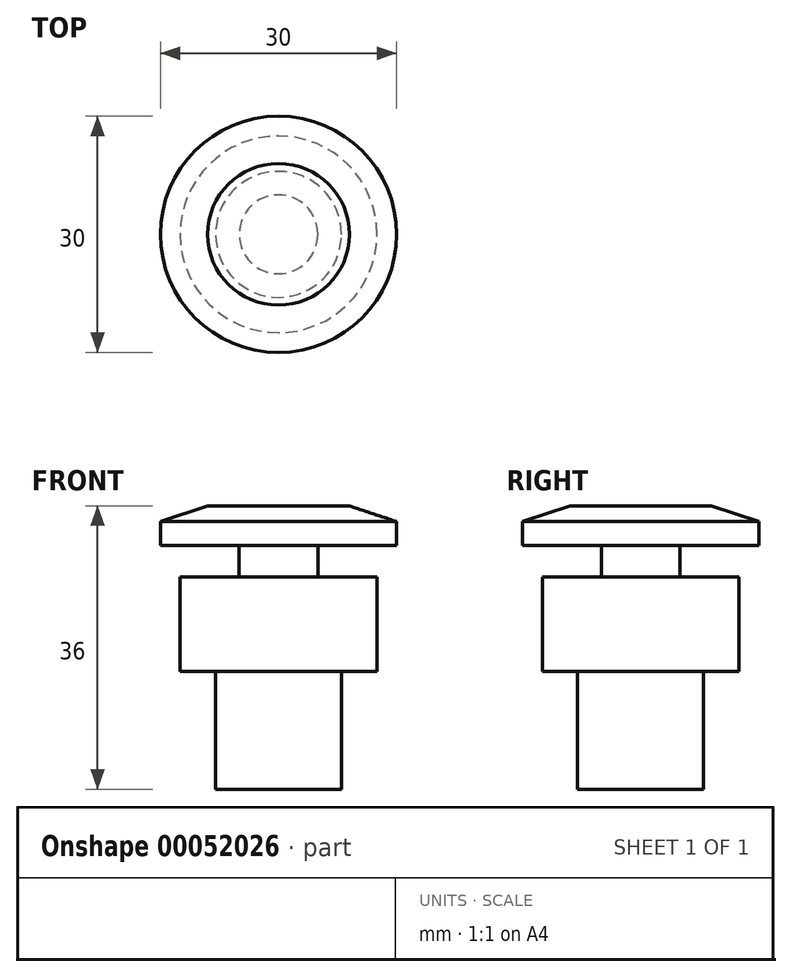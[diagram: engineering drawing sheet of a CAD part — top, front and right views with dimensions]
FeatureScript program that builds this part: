
annotation { "Feature Type Name" : "Feature", "Feature Type Description" : "" }
export const myFeature = defineFeature(function(context is Context, id is Id, definition is map)
    precondition{}
    {
        {
            var Q0;
            Q0=qCreatedBy(makeId("Top.planeOp"),FACE);
            var sketch = newSketch(context, id + "F0", { "sketchPlane" : qUnion([Q0])});
            skCircle(sketch, "E0", {"center": v(0, 0) * mm, "radius": 12.5 * mm});
            skSolve(sketch);
        }
        {
            var Q0;
            Q0=qSketchRegion(id+"F0",true);
            extrude(context, id + "F1", {"entities" : qUnion([Q0]), "depth" : 12 * mm});
        }
        {
            var Q0;
            Q0=makeQuery(id+"F1.opExtrude","CAP_FACE",FACE,{"disambiguationData":[OSD([sQuery(id+"F0.wireOp",EDGE,"E0")])],"isStart":true});
            var sketch = newSketch(context, id + "F2", { "sketchPlane" : qUnion([Q0])});
            skCircle(sketch, "E1", {"center": v(0, 0) * mm, "radius": 8 * mm});
            skSolve(sketch);
        }
        {
            var Q0;
            Q0=makeQuery(id+"F2.imprint","IMPRINT",FACE,{"disambiguationData":[TD([[makeQuery(id+"F2.imprint","IMPRINT",EDGE,{"derivedFrom":sQuery(id+"F2.wireOp",EDGE,"E1")}),1.0]])]});
            extrude(context, id + "F3", {"entities" : qUnion([Q0]), "operationType" : NewBodyOperationType.ADD, "depth" : 15 * mm});
        }
        {
            var Q0;
            Q0=makeQuery(id+"F1.opExtrude","CAP_FACE",FACE,{"disambiguationData":[OSD([sQuery(id+"F0.wireOp",EDGE,"E0")])],"isStart":false});
            var sketch = newSketch(context, id + "F4", { "sketchPlane" : qUnion([Q0])});
            skCircle(sketch, "E2", {"center": v(0, 0) * mm, "radius": 5 * mm});
            skSolve(sketch);
        }
        {
            var Q0;
            Q0=makeQuery(id+"F4.imprint","IMPRINT",FACE,{"disambiguationData":[TD([[makeQuery(id+"F4.imprint","IMPRINT",EDGE,{"derivedFrom":sQuery(id+"F4.wireOp",EDGE,"E2")}),1.0]])]});
            extrude(context, id + "F5", {"entities" : qUnion([Q0]), "operationType" : NewBodyOperationType.ADD, "depth" : 4 * mm});
        }
        {
            var Q0;
            Q0=makeQuery(id+"F5.opExtrude","CAP_FACE",FACE,{"disambiguationData":[OSD([sQuery(id+"F4.wireOp",EDGE,"E2")])],"isStart":false});
            var sketch = newSketch(context, id + "F6", { "sketchPlane" : qUnion([Q0])});
            skCircle(sketch, "E3", {"center": v(0, 0) * mm, "radius": 15 * mm});
            skSolve(sketch);
        }
        {
            var Q0;
            Q0=makeQuery(id+"F6.imprint","IMPRINT",FACE,{"disambiguationData":[TD([[makeQuery(id+"F6.imprint","IMPRINT",EDGE,{"derivedFrom":sQuery(id+"F6.wireOp",EDGE,"E3")}),1.0]])]});
            var Q1;
            Q1=makeQuery(id+"F6.imprint","IMPRINT",FACE,{"disambiguationData":[TD([[makeQuery(id+"F6.imprint","IMPRINT",EDGE,{"derivedFrom":makeQuery(id+"F5.opExtrude","CAP_EDGE",EDGE,{"disambiguationData":[OSD([sQuery(id+"F4.wireOp",EDGE,"E2")])],"isStart":false})}),1.0]])]});
            extrude(context, id + "F7", {"entities" : qUnion([Q0, Q1]), "operationType" : NewBodyOperationType.ADD, "depth" : 5 * mm});
        }
        {
            var Q0;
            Q0=makeQuery(id+"F7.opExtrude","CAP_EDGE",EDGE,{"disambiguationData":[OSD([sQuery(id+"F6.wireOp",EDGE,"E3")])],"isStart":false});
            chamfer(context, id + "F8", {"entities" : qUnion([Q0]), "chamferType" : ChamferType.TWO_OFFSETS, "width1" : 6 * mm, "oppositeDirection" : false, "width2" : 2 * mm, "tangentPropagation" : true});
        }
    });
